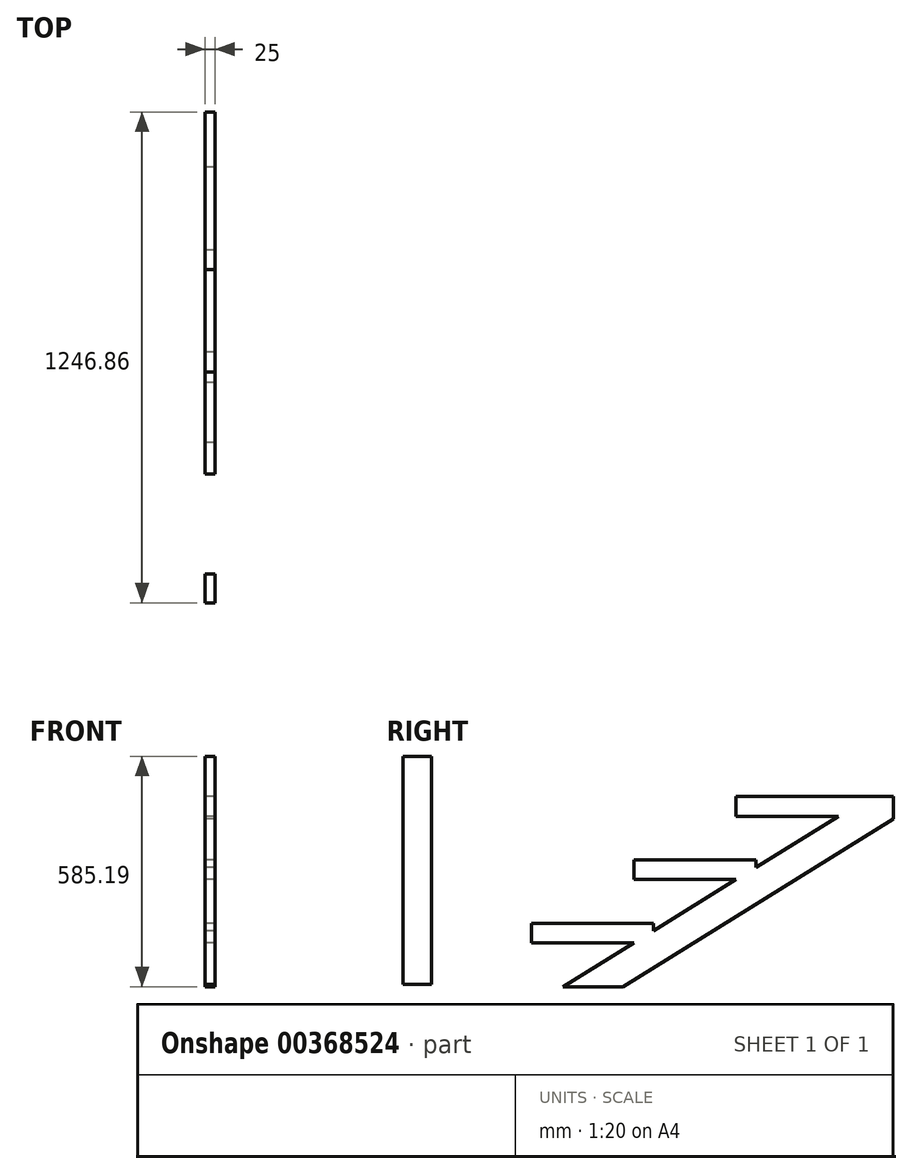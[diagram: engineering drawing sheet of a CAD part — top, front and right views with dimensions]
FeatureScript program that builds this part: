
annotation { "Feature Type Name" : "Feature", "Feature Type Description" : "" }
export const myFeature = defineFeature(function(context is Context, id is Id, definition is map)
    precondition{}
    {
        {
            var Q0;
            Q0=qCreatedBy(makeId("Right.planeOp"),FACE);
            var sketch = newSketch(context, id + "F0", { "sketchPlane" : qUnion([Q0])});
            skLineSegment(sketch, "E0.bottom", {"start": v(0, 0) * mm, "end": v(260, 0) * mm});
            skLineSegment(sketch, "E0.top", {"start": v(0, 50) * mm, "end": v(260, 50) * mm});
            skLineSegment(sketch, "E0.left", {"start": v(0, 0) * mm, "end": v(0, 50) * mm});
            skLineSegment(sketch, "E0.right", {"start": v(260, 0) * mm, "end": v(260, 50) * mm});
            skLineSegment(sketch, "E1.bottom", {"start": v(260, 50) * mm, "end": v(310, 50) * mm});
            skLineSegment(sketch, "E1.top", {"start": v(260, 0) * mm, "end": v(310, 0) * mm});
            skLineSegment(sketch, "E1.left", {"start": v(260, 50) * mm, "end": v(260, 0) * mm});
            skLineSegment(sketch, "E1.right", {"start": v(310, 50) * mm, "end": v(310, 0) * mm});
            skLineSegment(sketch, "E2.bottom", {"start": v(260, 161) * mm, "end": v(520, 161) * mm});
            skLineSegment(sketch, "E2.top", {"start": v(260, 211) * mm, "end": v(520, 211) * mm});
            skLineSegment(sketch, "E2.left", {"start": v(260, 161) * mm, "end": v(260, 211) * mm});
            skLineSegment(sketch, "E2.right", {"start": v(520, 161) * mm, "end": v(520, 211) * mm});
            skLineSegment(sketch, "E3.bottom", {"start": v(520, 211) * mm, "end": v(570, 211) * mm});
            skLineSegment(sketch, "E3.top", {"start": v(520, 161) * mm, "end": v(570, 161) * mm});
            skLineSegment(sketch, "E3.left", {"start": v(520, 211) * mm, "end": v(520, 161) * mm});
            skLineSegment(sketch, "E3.right", {"start": v(570, 211) * mm, "end": v(570, 161) * mm});
            skLineSegment(sketch, "E4", {"start": v(260, 0) * mm, "end": v(520, 161) * mm});
            skLineSegment(sketch, "E5", {"start": v(520, 161) * mm, "end": v(780, 322) * mm});
            skLineSegment(sketch, "E6", {"start": v(260, 0) * mm, "end": v(80.75, -111) * mm});
            skLineSegment(sketch, "E7", {"start": v(80.75, -111) * mm, "end": v(531.1, -111) * mm});
            skLineSegment(sketch, "E8.0", {"start": v(302.12, -68.02) * mm, "end": v(232.7, -111) * mm});
            skLineSegment(sketch, "E8.1", {"start": v(302.12, -68.02) * mm, "end": v(562.12, 92.98) * mm});
            skLineSegment(sketch, "E8.2", {"start": v(562.12, 92.98) * mm, "end": v(920, 314.6) * mm});
            skLineSegment(sketch, "E9.bottom", {"start": v(520, 372) * mm, "end": v(920, 372) * mm});
            skLineSegment(sketch, "E9.top", {"start": v(520, 322) * mm, "end": v(920, 322) * mm});
            skLineSegment(sketch, "E9.left", {"start": v(520, 372) * mm, "end": v(520, 322) * mm});
            skLineSegment(sketch, "E9.right", {"start": v(920, 372) * mm, "end": v(920, 322) * mm});
            skLineSegment(sketch, "E10", {"start": v(920, 322) * mm, "end": v(920, 269.83) * mm});
            skLineSegment(sketch, "E11", {"start": v(80.75, -111) * mm, "end": v(-253.64, -111) * mm, "construction": true});
            skLineSegment(sketch, "E12", {"start": v(-253.64, -111) * mm, "end": v(-253.64, 474.2) * mm});
            skLineSegment(sketch, "E13.bottom", {"start": v(-253.64, 474.2) * mm, "end": v(-326.86, 474.2) * mm});
            skLineSegment(sketch, "E13.top", {"start": v(-253.64, -104.85) * mm, "end": v(-326.86, -104.85) * mm});
            skLineSegment(sketch, "E13.left", {"start": v(-253.64, 474.2) * mm, "end": v(-253.64, -104.85) * mm});
            skLineSegment(sketch, "E13.right", {"start": v(-326.86, 474.2) * mm, "end": v(-326.86, -104.85) * mm});
            skSolve(sketch);
        }
        {
            var Q0;
            Q0 = qSketchRegion(id + "F0", true);
            extrude(context, id + "F1", {"entities" : qUnion([Q0]), "depth" : 25 * mm});
        }
    });
